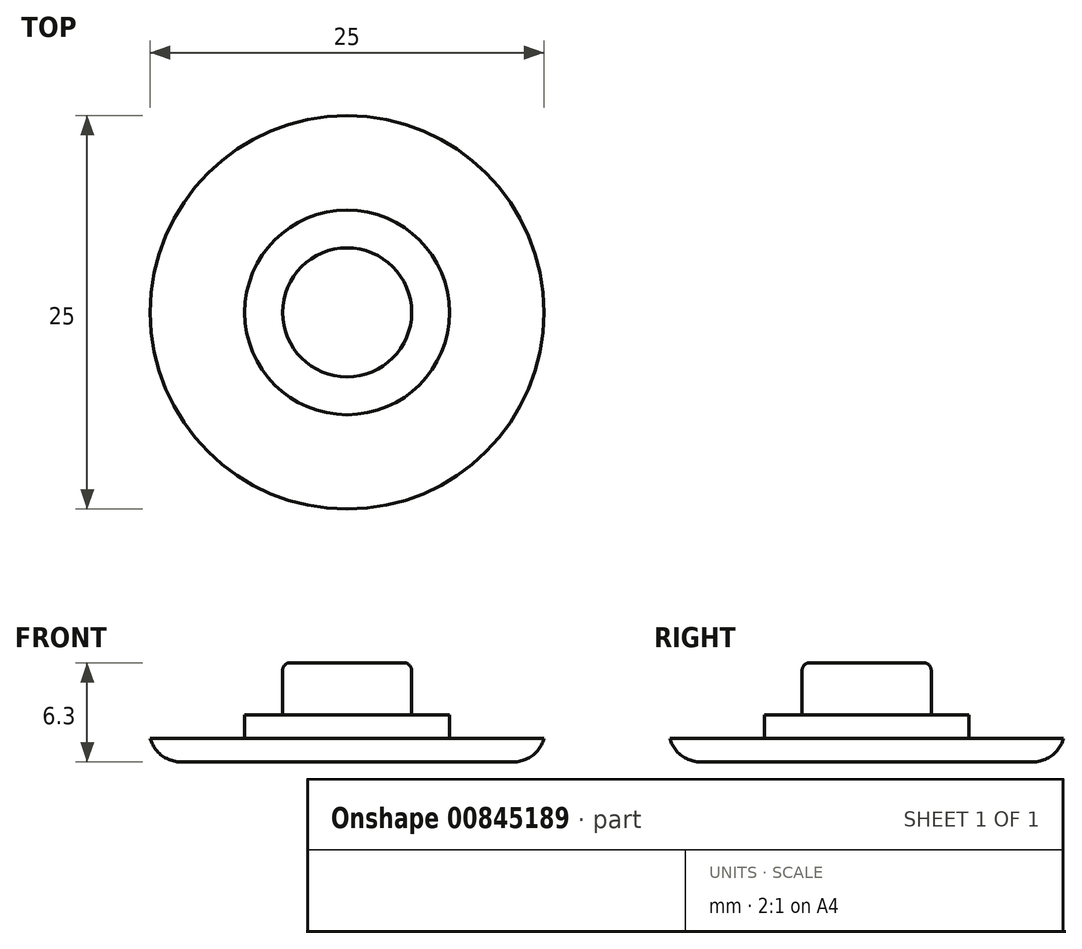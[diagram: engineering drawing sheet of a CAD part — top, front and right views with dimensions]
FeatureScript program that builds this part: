
annotation { "Feature Type Name" : "Feature", "Feature Type Description" : "" }
export const myFeature = defineFeature(function(context is Context, id is Id, definition is map)
    precondition{}
    {
        {
            var Q0;
            Q0=qCreatedBy(makeId("Top.planeOp"),FACE);
            var sketch = newSketch(context, id + "F0", { "sketchPlane" : qUnion([Q0])});
            skCircle(sketch, "E0", {"center": v(0, 0) * mm, "radius": 12.5 * mm});
            skCircle(sketch, "E1", {"center": v(0, 0) * mm, "radius": 6.5 * mm});
            skCircle(sketch, "E2", {"center": v(0, 0) * mm, "radius": 4.1 * mm});
            skSolve(sketch);
        }
        {
            var Q0;
            Q0=makeQuery(id+"F0.imprint","IMPRINT",FACE,{"disambiguationData":[TD([[makeQuery(id+"F0.imprint","IMPRINT",EDGE,{"derivedFrom":sQuery(id+"F0.wireOp",EDGE,"E2")}),1.0]])]});
            var Q1;
            Q1=makeQuery(id+"F0.imprint","IMPRINT",FACE,{"disambiguationData":[TD([[makeQuery(id+"F0.imprint","IMPRINT",EDGE,{"derivedFrom":sQuery(id+"F0.wireOp",EDGE,"fb282312-d634-4574-8ab1-5dd5f74cf45d0.MirrorC")}),-1.0]])]});
            extrude(context, id + "F1", {"entities" : qUnion([Q0, Q1]), "depth" : (3.3 + 3) * mm, "offsetDistance" : 25 * mm});
        }
        {
            var Q0;
            Q0=makeQuery(id+"F0.imprint","IMPRINT",FACE,{"disambiguationData":[TD([[makeQuery(id+"F0.imprint","IMPRINT",EDGE,{"derivedFrom":sQuery(id+"F0.wireOp",EDGE,"E1")}),1.0]])]});
            var Q1;
            Q1=makeQuery(id+"F0.imprint","IMPRINT",FACE,{"disambiguationData":[TD([[makeQuery(id+"F0.imprint","IMPRINT",EDGE,{"derivedFrom":sQuery(id+"F0.wireOp",EDGE,"fb282312-d634-4574-8ab1-5dd5f74cf45d0.MirrorC")}),1.0]])]});
            extrude(context, id + "F2", {"entities" : qUnion([Q0, Q1]), "operationType" : NewBodyOperationType.ADD, "depth" : 3 * mm, "offsetDistance" : 25 * mm});
        }
        {
            var Q0;
            Q0=makeQuery(id+"F0.imprint","IMPRINT",FACE,{"disambiguationData":[TD([[makeQuery(id+"F0.imprint","IMPRINT",EDGE,{"derivedFrom":sQuery(id+"F0.wireOp",EDGE,"E0")}),1.0]])]});
            var Q1;
            Q1=makeQuery(id+"F0.imprint","IMPRINT",FACE,{"disambiguationData":[TD([[makeQuery(id+"F0.imprint","IMPRINT",EDGE,{"derivedFrom":sQuery(id+"F0.wireOp",EDGE,"fb282312-d634-4574-8ab1-5dd5f74cf45d1.MirrorC")}),-1.0]])]});
            extrude(context, id + "F3", {"entities" : qUnion([Q0, Q1]), "operationType" : NewBodyOperationType.ADD, "depth" : 1.5 * mm, "offsetDistance" : 25 * mm});
        }
        {
            var Q0;
            Q0=makeQuery(id+"F1.opExtrude","CAP_EDGE",EDGE,{"disambiguationData":[OSD([sQuery(id+"F0.wireOp",EDGE,"E2")])],"isStart":false});
            fillet(context, id + "F4", {"entities" : qUnion([Q0]), "radius" : .5 * mm, "tangentPropagation" : true, "allowEdgeOverflow" : false});
        }
        {
            var Q0;
            Q0=makeQuery(id+"F3.opExtrude","CAP_EDGE",EDGE,{"disambiguationData":[OSD([sQuery(id+"F0.wireOp",EDGE,"E0")])],"isStart":true});
            var Q1;
            Q1=makeQuery(id+"F3.opExtrude","CAP_EDGE",EDGE,{"disambiguationData":[OSD([sQuery(id+"F0.wireOp",EDGE,"fb282312-d634-4574-8ab1-5dd5f74cf45d1.MirrorC")])],"isStart":true});
            fillet(context, id + "F5", {"entities" : qUnion([Q0, Q1]), "radius" : 2 * mm, "tangentPropagation" : true, "allowEdgeOverflow" : false});
        }
    });
